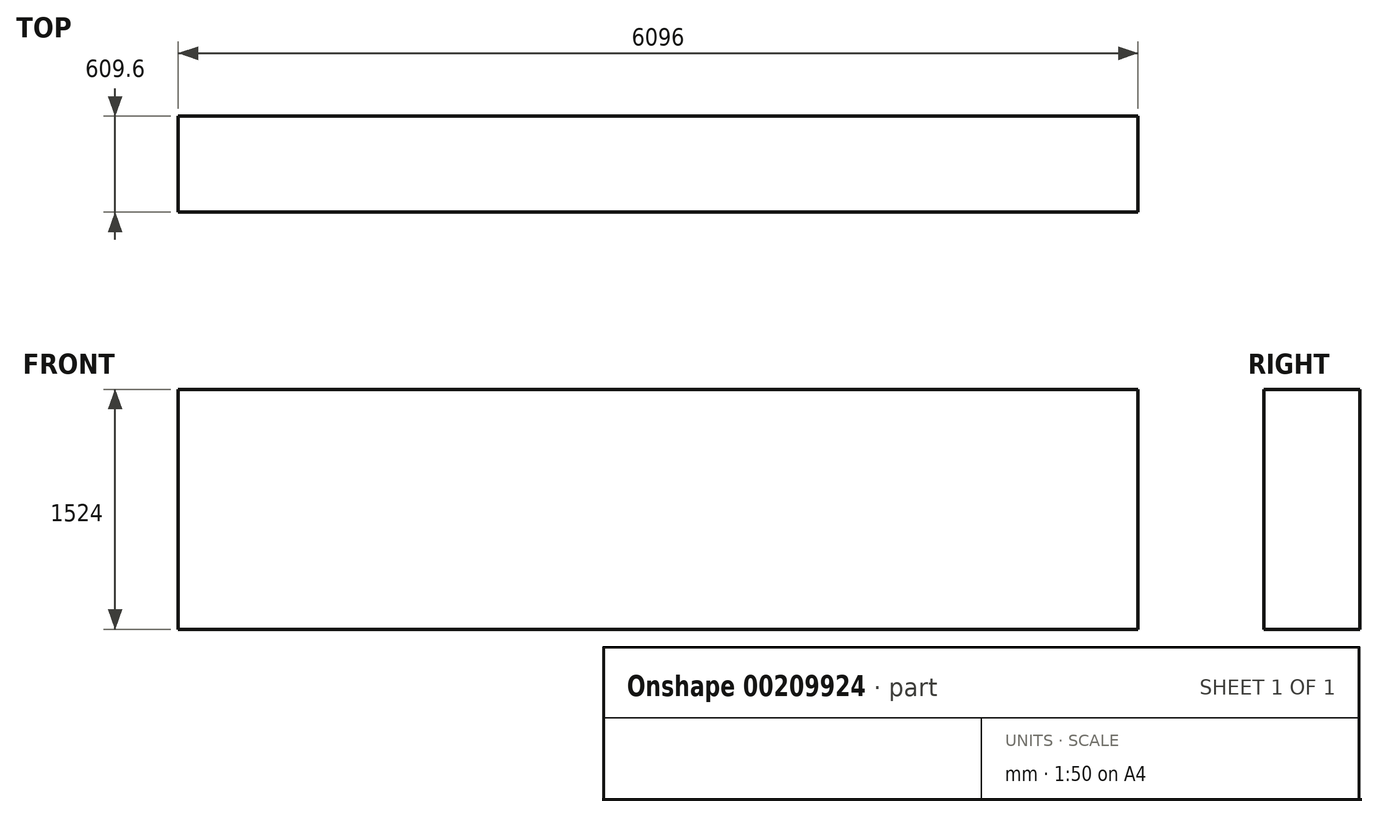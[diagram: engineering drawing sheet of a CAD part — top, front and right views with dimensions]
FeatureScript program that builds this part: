
annotation { "Feature Type Name" : "Feature", "Feature Type Description" : "" }
export const myFeature = defineFeature(function(context is Context, id is Id, definition is map)
    precondition{}
    {
        {
            var Q0;
            Q0=qCreatedBy(makeId("Top.planeOp"),FACE);
            var sketch = newSketch(context, id + "F0", { "sketchPlane" : qUnion([Q0])});
            skLineSegment(sketch, "E0.bottom", {"start": v(-3045.22, -186.75) * mm, "end": v(3050.78, -186.75) * mm});
            skLineSegment(sketch, "E0.top", {"start": v(-3045.22, -796.35) * mm, "end": v(3050.78, -796.35) * mm});
            skLineSegment(sketch, "E0.left", {"start": v(-3045.22, -186.75) * mm, "end": v(-3045.22, -796.35) * mm});
            skLineSegment(sketch, "E0.right", {"start": v(3050.78, -186.75) * mm, "end": v(3050.78, -796.35) * mm});
            skSolve(sketch);
        }
        {
            var Q0;
            Q0 = qSketchRegion(id + "F0", true);
            extrude(context, id + "F1", {"entities" : qUnion([Q0]), "depth" : 1524 * mm});
        }
    });
